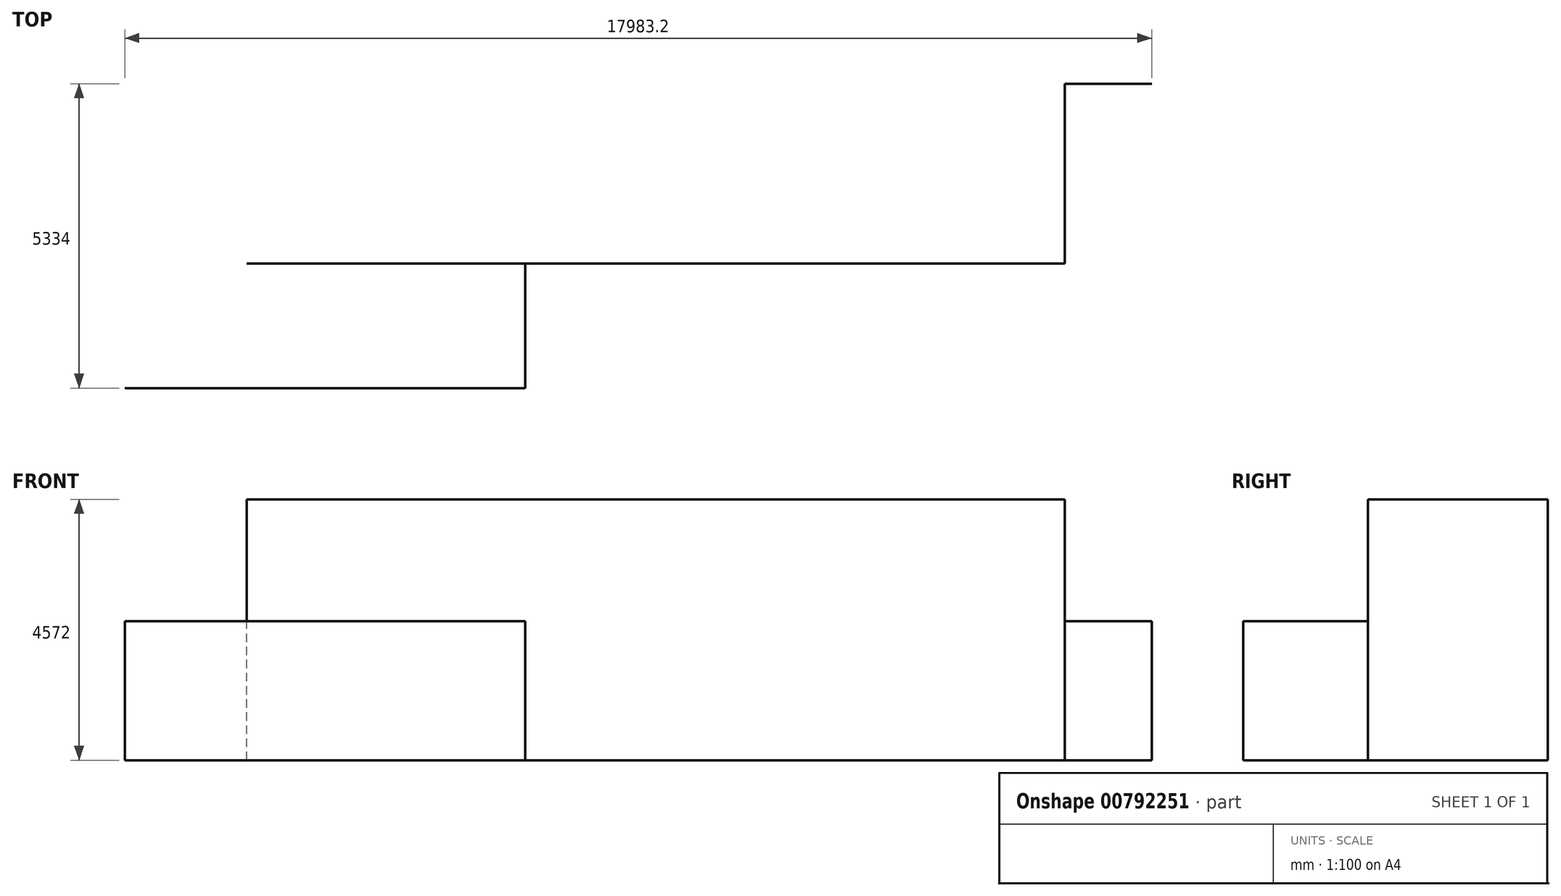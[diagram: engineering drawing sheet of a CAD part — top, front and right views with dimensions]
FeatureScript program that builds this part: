
annotation { "Feature Type Name" : "Feature", "Feature Type Description" : "" }
export const myFeature = defineFeature(function(context is Context, id is Id, definition is map)
    precondition{}
    {
        {
            var Q0;
            Q0=qCreatedBy(makeId("Top.planeOp"),FACE);
            var sketch = newSketch(context, id + "F0", { "sketchPlane" : qUnion([Q0])});
            skLineSegment(sketch, "E0", {"start": v(0, 6553.2) * mm, "end": v(0, 0) * mm});
            skLineSegment(sketch, "E1", {"start": v(0, 6553.2) * mm, "end": v(7010.4, 6553.2) * mm});
            skLineSegment(sketch, "E2", {"start": v(11125.2, 6553.2) * mm, "end": v(11125.2, 0) * mm});
            skLineSegment(sketch, "E3", {"start": v(0, 0) * mm, "end": v(11125.2, 0) * mm});
            skLineSegment(sketch, "E4", {"start": v(11125.2, 0) * mm, "end": v(16459.2, 0) * mm});
            skLineSegment(sketch, "E5", {"start": v(16459.2, 0) * mm, "end": v(16459.2, 8737.6) * mm});
            skLineSegment(sketch, "E6", {"start": v(2133.6, 6553.2) * mm, "end": v(2133.6, 6553.2) * mm});
            skLineSegment(sketch, "E7", {"start": v(7010.4, 6553.2) * mm, "end": v(7010.4, 8737.6) * mm});
            skLineSegment(sketch, "E8", {"start": v(2133.6, 8737.6) * mm, "end": v(11125.2, 8737.6) * mm});
            skPoint(sketch, "E9", {"position": v(7010.4, 6489.7) * mm});
            skLineSegment(sketch, "E10", {"start": v(7010.4, 6553.2) * mm, "end": v(11125.2, 6553.2) * mm});
            skLineSegment(sketch, "E11", {"start": v(2133.6, 6553.2) * mm, "end": v(2133.6, 8737.6) * mm});
            skLineSegment(sketch, "E12", {"start": v(16459.2, 0) * mm, "end": v(17983.2, 0) * mm});
            skLineSegment(sketch, "E13", {"start": v(17983.2, 0) * mm, "end": v(17983.2, 11887.2) * mm});
            skLineSegment(sketch, "E14", {"start": v(17983.2, 11887.2) * mm, "end": v(16459.2, 11887.2) * mm});
            skLineSegment(sketch, "E15", {"start": v(16459.2, 11887.2) * mm, "end": v(16459.2, 8737.6) * mm});
            skLineSegment(sketch, "E16", {"start": v(11125.2, 6553.2) * mm, "end": v(11125.2, 8737.6) * mm});
            skLineSegment(sketch, "E17", {"start": v(11125.2, 8737.6) * mm, "end": v(16459.2, 8737.6) * mm});
            skEllipticalArc(sketch, "E18", {});
            skLineSegment(sketch, "E19", {"start": v(0, 0) * mm, "end": v(0, 609.6) * mm});
            skLineSegment(sketch, "E20", {"start": v(0, 609.6) * mm, "end": v(11125.2, 609.6) * mm});
            skLineSegment(sketch, "E21", {"start": v(11125.2, 609.6) * mm, "end": v(11125.2, 0) * mm});
            skPoint(sketch, "E22", {"position": v(5562.6, 609.6) * mm});
            skEllipticalArc(sketch, "E23.1.0.0", {});
            skLineSegment(sketch, "E23.direction1", {"start": v(3733.8, 3652.53) * mm, "end": v(7391.4, 3652.53) * mm, "construction": true});
            skPoint(sketch, "E24.visualSharp", {"position": v(5562.6, 4841.25) * mm});
            skArc(sketch, "E24.filletArc", {"start": v(5361.4, 5043.71) * mm, "mid": v(5562.6, 4967.87) * mm, "end": v(5763.8, 5043.71) * mm});
            skPoint(sketch, "E25.visualSharp", {"position": v(5562.6, 2463.8) * mm});
            skArc(sketch, "E25.filletArc", {"start": v(5763.8, 2261.34) * mm, "mid": v(5562.6, 2337.18) * mm, "end": v(5361.4, 2261.34) * mm});
            skLineSegment(sketch, "E26.bottom", {"start": v(0, 6616.7) * mm, "end": v(127, 6616.7) * mm});
            skLineSegment(sketch, "E26.top", {"start": v(0, 6489.7) * mm, "end": v(127, 6489.7) * mm});
            skLineSegment(sketch, "E26.left", {"start": v(0, 6616.7) * mm, "end": v(0, 6489.7) * mm});
            skLineSegment(sketch, "E26.right", {"start": v(127, 6616.7) * mm, "end": v(127, 6489.7) * mm});
            skLineSegment(sketch, "E27.1.0.0", {"start": v(2438.4, 6489.7) * mm, "end": v(2565.4, 6489.7) * mm});
            skLineSegment(sketch, "E27.1.0.1", {"start": v(2438.4, 6616.7) * mm, "end": v(2565.4, 6616.7) * mm});
            skLineSegment(sketch, "E27.1.0.2", {"start": v(2565.4, 6616.7) * mm, "end": v(2565.4, 6489.7) * mm});
            skLineSegment(sketch, "E27.1.0.3", {"start": v(2438.4, 6616.7) * mm, "end": v(2438.4, 6489.7) * mm});
            skLineSegment(sketch, "E27.2.0.0", {"start": v(4876.8, 6489.7) * mm, "end": v(5003.8, 6489.7) * mm});
            skLineSegment(sketch, "E27.2.0.1", {"start": v(4876.8, 6616.7) * mm, "end": v(5003.8, 6616.7) * mm});
            skLineSegment(sketch, "E27.2.0.2", {"start": v(5003.8, 6616.7) * mm, "end": v(5003.8, 6489.7) * mm});
            skLineSegment(sketch, "E27.2.0.3", {"start": v(4876.8, 6616.7) * mm, "end": v(4876.8, 6489.7) * mm});
            skLineSegment(sketch, "E27.direction1", {"start": v(0, 6489.7) * mm, "end": v(2438.4, 6489.7) * mm, "construction": true});
            skLineSegment(sketch, "E28.2.0.0", {"start": v(7010.4, 6489.7) * mm, "end": v(7137.4, 6489.7) * mm});
            skLineSegment(sketch, "E28.2.0.1", {"start": v(7010.4, 6616.7) * mm, "end": v(7137.4, 6616.7) * mm});
            skLineSegment(sketch, "E28.2.0.2", {"start": v(7137.4, 6616.7) * mm, "end": v(7137.4, 6489.7) * mm});
            skLineSegment(sketch, "E28.2.0.3", {"start": v(7010.4, 6616.7) * mm, "end": v(7010.4, 6489.7) * mm});
            const initialGuessF0  = {"E18": [3.7338, 3.652526617050171, 1, 0, 2.286, 1.9812, 0.778472991607, 5.504712315572586], "E23.1.0.0": [7.3914, 3.6525266170501713, 1, 0, 2.286, 1.9812, 3.9200656451967903, 2.363119661982793]};
            skSetInitialGuess(sketch, initialGuessF0);
            skSolve(sketch);
        }
        {
            var Q0;
            Q0=sQuery(id+"F0.wireOp",EDGE,"E1");
            extrude(context, id + "F1", {"bodyType" : ToolBodyType.SURFACE, "surfaceEntities" : qUnion([Q0]), "depth" : 2438.4 * mm, "offsetDistance" : 30.48 * mm});
        }
        {
            var Q0;
            Q0=sQuery(id+"F0.wireOp",EDGE,"E7");
            extrude(context, id + "F2", {"bodyType" : ToolBodyType.SURFACE, "surfaceEntities" : qUnion([Q0]), "depth" : 2438.4 * mm, "offsetDistance" : 30.48 * mm});
        }
        {
            var Q0;
            Q0=sQuery(id+"F0.wireOp",EDGE,"E8");
            var Q1;
            Q1=sQuery(id+"F0.wireOp",EDGE,"E17");
            extrude(context, id + "F3", {"bodyType" : ToolBodyType.SURFACE, "surfaceEntities" : qUnion([Q0, Q1]), "depth" : 4572 * mm, "offsetDistance" : 30.48 * mm});
        }
        {
            var Q0;
            Q0=sQuery(id+"F0.wireOp",EDGE,"E15");
            extrude(context, id + "F4", {"bodyType" : ToolBodyType.SURFACE, "surfaceEntities" : qUnion([Q0]), "depth" : 4572 * mm, "offsetDistance" : 30.48 * mm});
        }
        {
            var Q0;
            Q0=sQuery(id+"F0.wireOp",EDGE,"E14");
            extrude(context, id + "F5", {"bodyType" : ToolBodyType.SURFACE, "surfaceEntities" : qUnion([Q0]), "depth" : 2438.4 * mm, "offsetDistance" : 30.48 * mm});
        }
    });
